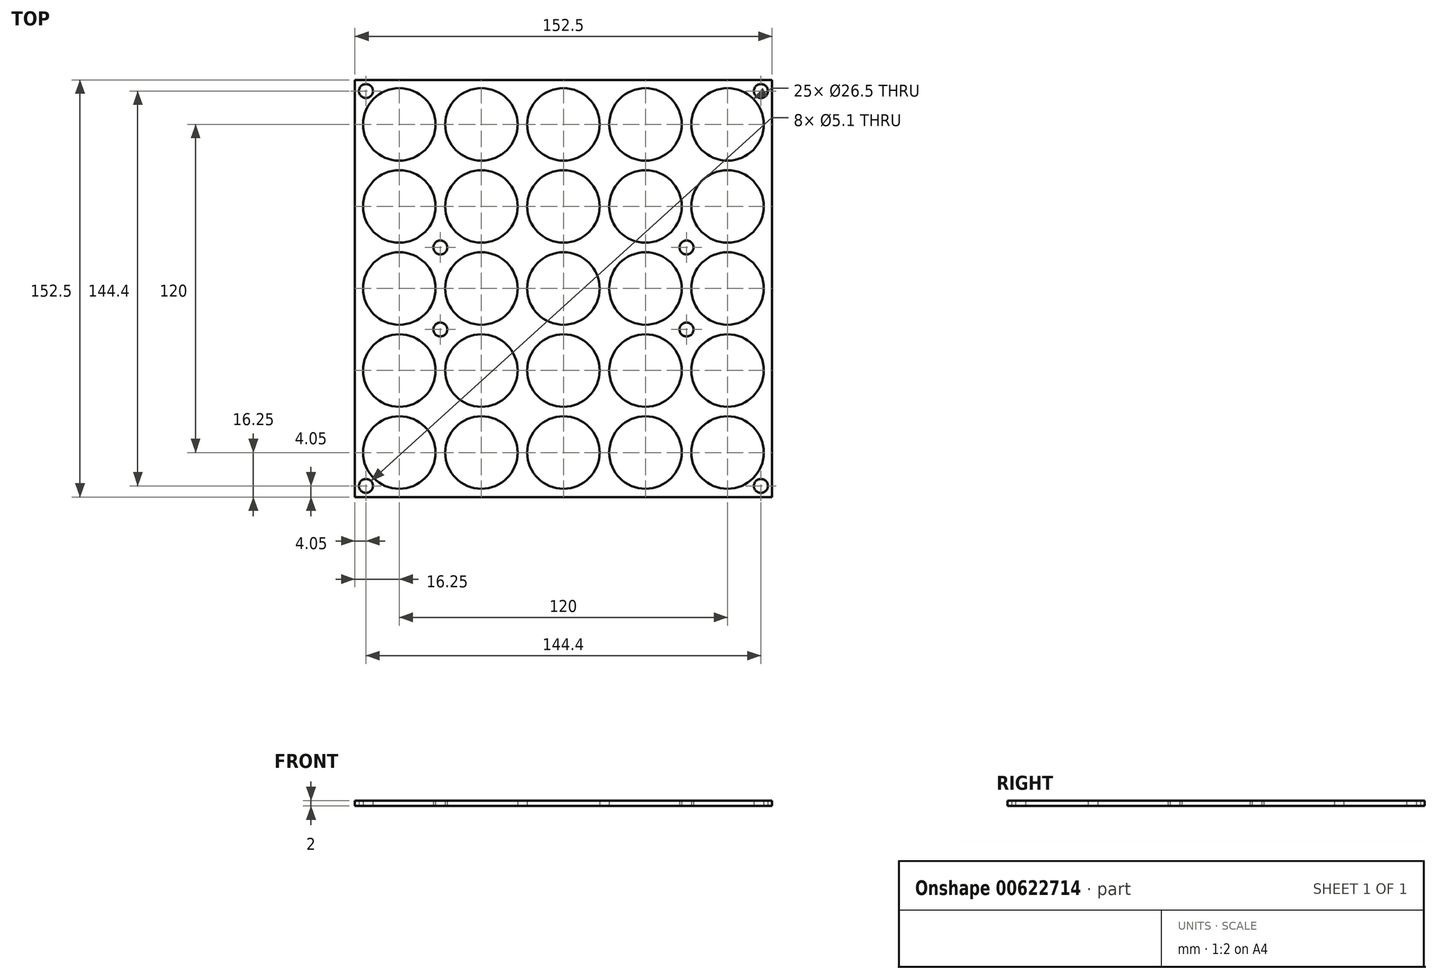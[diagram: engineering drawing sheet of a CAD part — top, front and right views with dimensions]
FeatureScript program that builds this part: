
annotation { "Feature Type Name" : "Feature", "Feature Type Description" : "" }
export const myFeature = defineFeature(function(context is Context, id is Id, definition is map)
    precondition{}
    {
        {
            var Q0;
            Q0=qCreatedBy(makeId("Top.planeOp"),FACE);
            var sketch = newSketch(context, id + "F0", { "sketchPlane" : qUnion([Q0])});
            skLineSegment(sketch, "E0.bottom", {"start": v(-76.25, 76.25) * mm, "end": v(76.25, 76.25) * mm});
            skLineSegment(sketch, "E0.top", {"start": v(-76.25, -76.25) * mm, "end": v(76.25, -76.25) * mm});
            skLineSegment(sketch, "E0.left", {"start": v(-76.25, 76.25) * mm, "end": v(-76.25, -76.25) * mm});
            skLineSegment(sketch, "E0.right", {"start": v(76.25, 76.25) * mm, "end": v(76.25, -76.25) * mm});
            skPoint(sketch, "E0.middle", {"position": v(0, 0) * mm});
            skCircle(sketch, "E1", {"center": v(-60, 60) * mm, "radius": 13.25 * mm});
            skCircle(sketch, "E2.0.1.0", {"center": v(-60, 30) * mm, "radius": 13.25 * mm});
            skCircle(sketch, "E2.0.2.0", {"center": v(-60, 0) * mm, "radius": 13.25 * mm});
            skCircle(sketch, "E2.0.3.0", {"center": v(-60, -30) * mm, "radius": 13.25 * mm});
            skCircle(sketch, "E2.1.0.0", {"center": v(-30, 60) * mm, "radius": 13.25 * mm});
            skCircle(sketch, "E2.1.1.0", {"center": v(-30, 30) * mm, "radius": 13.25 * mm});
            skCircle(sketch, "E2.1.2.0", {"center": v(-30, 0) * mm, "radius": 13.25 * mm});
            skCircle(sketch, "E2.1.3.0", {"center": v(-30, -30) * mm, "radius": 13.25 * mm});
            skCircle(sketch, "E2.2.0.0", {"center": v(0, 60) * mm, "radius": 13.25 * mm});
            skCircle(sketch, "E2.2.1.0", {"center": v(0, 30) * mm, "radius": 13.25 * mm});
            skCircle(sketch, "E2.2.2.0", {"center": v(0, 0) * mm, "radius": 13.25 * mm});
            skCircle(sketch, "E2.2.3.0", {"center": v(0, -30) * mm, "radius": 13.25 * mm});
            skCircle(sketch, "E2.3.0.0", {"center": v(30, 60) * mm, "radius": 13.25 * mm});
            skCircle(sketch, "E2.3.1.0", {"center": v(30, 30) * mm, "radius": 13.25 * mm});
            skCircle(sketch, "E2.3.2.0", {"center": v(30, 0) * mm, "radius": 13.25 * mm});
            skCircle(sketch, "E2.3.3.0", {"center": v(30, -30) * mm, "radius": 13.25 * mm});
            skCircle(sketch, "E2.4.0.0", {"center": v(60, 60) * mm, "radius": 13.25 * mm});
            skCircle(sketch, "E2.4.1.0", {"center": v(60, 30) * mm, "radius": 13.25 * mm});
            skCircle(sketch, "E2.4.2.0", {"center": v(60, 0) * mm, "radius": 13.25 * mm});
            skCircle(sketch, "E2.4.3.0", {"center": v(60, -30) * mm, "radius": 13.25 * mm});
            skLineSegment(sketch, "E2.direction1", {"start": v(-60, 60) * mm, "end": v(-30, 60) * mm, "construction": true});
            skLineSegment(sketch, "E2.direction2", {"start": v(-60, 60) * mm, "end": v(-60, 30) * mm, "construction": true});
            skLineSegment(sketch, "E3", {"start": v(0, 88.74) * mm, "end": v(0, -97.9) * mm, "construction": true});
            skLineSegment(sketch, "E4", {"start": v(-96.24, 0) * mm, "end": v(100.37, 0) * mm, "construction": true});
            skCircle(sketch, "E5", {"center": v(-45, 15) * mm, "radius": 2.55 * mm});
            skCircle(sketch, "E6", {"center": v(-72.2, 72.2) * mm, "radius": 2.55 * mm});
            skCircle(sketch, "E7.MirrorC", {"center": v(45, 15) * mm, "radius": 2.55 * mm});
            skCircle(sketch, "E8.MirrorC", {"center": v(72.2, 72.2) * mm, "radius": 2.55 * mm});
            skCircle(sketch, "E9.MirrorC", {"center": v(-45, -15) * mm, "radius": 2.55 * mm});
            skCircle(sketch, "E10.MirrorC", {"center": v(-72.2, -72.2) * mm, "radius": 2.55 * mm});
            skCircle(sketch, "E11.MirrorC", {"center": v(72.2, -72.2) * mm, "radius": 2.55 * mm});
            skCircle(sketch, "E12.MirrorC", {"center": v(45, -15) * mm, "radius": 2.55 * mm});
            skCircle(sketch, "E13.0.0.4", {"center": v(-60, -60) * mm, "radius": 13.25 * mm});
            skCircle(sketch, "E13.0.1.4", {"center": v(-30, -60) * mm, "radius": 13.25 * mm});
            skCircle(sketch, "E13.0.2.4", {"center": v(0, -60) * mm, "radius": 13.25 * mm});
            skCircle(sketch, "E13.0.3.4", {"center": v(30, -60) * mm, "radius": 13.25 * mm});
            skCircle(sketch, "E13.0.4.4", {"center": v(60, -60) * mm, "radius": 13.25 * mm});
            skSolve(sketch);
        }
        {
            var Q0;
            Q0=makeQuery(id+"F0.imprint","IMPRINT",FACE,{"disambiguationData":[TD([[makeQuery(id+"F0.imprint","IMPRINT",EDGE,{"derivedFrom":sQuery(id+"F0.wireOp",EDGE,"E0.bottom")}),-1.0]])]});
            extrude(context, id + "F1", {"entities" : qUnion([Q0]), "depth" : 2 * mm, "offsetDistance" : 25 * mm});
        }
    });
